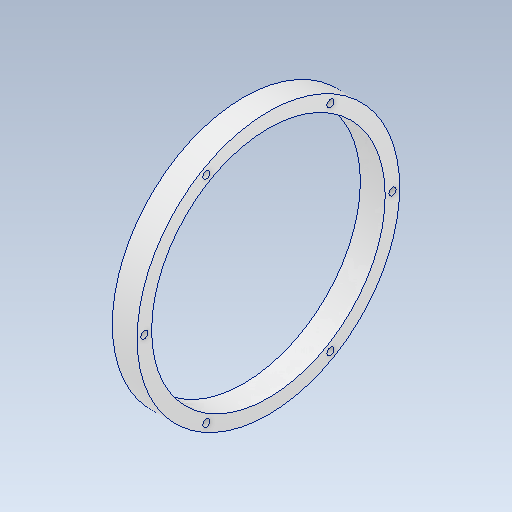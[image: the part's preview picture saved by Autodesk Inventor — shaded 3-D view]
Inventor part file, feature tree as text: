
AUTODESK INVENTOR PART (.ipt)
format: ipt  version: 2021 (Build 250183000, 183)  size: 148,480 bytes
history: native  units: mm
features: sketch x2, revolve x1, hole x1, pattern_circular x1, projected_geometry x1
ambient origin geometry x8: Origin, YZ Plane, XZ Plane, XY Plane, X Axis, Y Axis, Z Axis, Center Point
bodies: Solid1 (feature_tree)
feature tree (6):
  revolve  "Revolution1"  [1 undecoded]
  hole  "Hole1"  [1 undecoded]
  pattern_circular  "Circular Pattern1"  [2 undecoded]
  sketch  "Sketch1"  dims[d11=90.0deg d30=15.4mm]
  sketch  "Sketch2"  dims[d31=9.0mm d33=4.5mm d34=4.5mm d35=4.5mm d36=8.0mm d37=9.4mm d38=2.0mm d39=90.0deg d40=8.0mm d41=20.594885mm d42=60.0mm d43=360.0deg d47=72.5mm]
  projected_geometry  "Projected Loop1"
note: 4 required parameter values undecoded (feature->parameter linkage not recoverable at this tier; creation-order binding heuristic only, values carry confidence <= 0.55)